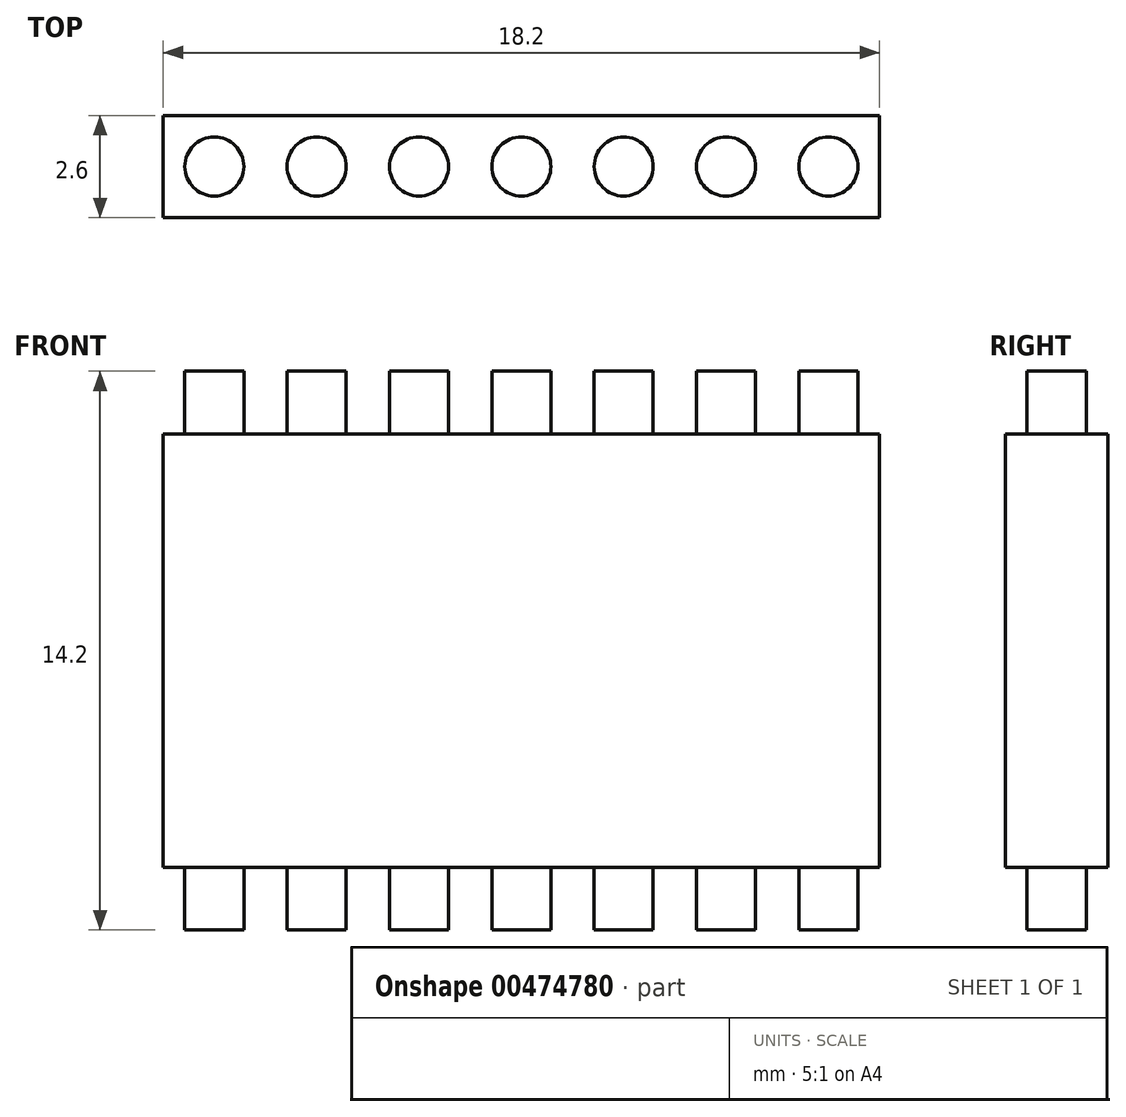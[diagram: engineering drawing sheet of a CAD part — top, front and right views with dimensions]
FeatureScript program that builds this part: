
annotation { "Feature Type Name" : "Feature", "Feature Type Description" : "" }
export const myFeature = defineFeature(function(context is Context, id is Id, definition is map)
    precondition{}
    {
        {
            var Q0;
            Q0=qCreatedBy(makeId("Top.planeOp"),FACE);
            var sketch = newSketch(context, id + "F0", { "sketchPlane" : qUnion([Q0])});
            skLineSegment(sketch, "E0.bottom", {"start": v(0, 0) * mm, "end": v(18.2, 0) * mm});
            skLineSegment(sketch, "E0.top", {"start": v(0, 2.6) * mm, "end": v(18.2, 2.6) * mm});
            skLineSegment(sketch, "E0.left", {"start": v(0, 0) * mm, "end": v(0, 2.6) * mm});
            skLineSegment(sketch, "E0.right", {"start": v(18.2, 0) * mm, "end": v(18.2, 2.6) * mm});
            skSolve(sketch);
        }
        {
            var Q0;
            Q0 = qSketchRegion(id + "F0", true);
            extrude(context, id + "F1", {"entities" : qUnion([Q0]), "depth" : 11 * mm});
        }
        {
            var Q0;
            Q0=makeQuery(id+"F1.opExtrude","CAP_FACE",FACE,{"disambiguationData":[OSD([sQuery(id+"F0.wireOp",EDGE,"E0.bottom"),sQuery(id+"F0.wireOp",EDGE,"E0.top"),sQuery(id+"F0.wireOp",EDGE,"E0.left"),sQuery(id+"F0.wireOp",EDGE,"E0.right")])],"isStart":false});
            var sketch = newSketch(context, id + "F2", { "sketchPlane" : qUnion([Q0])});
            skLineSegment(sketch, "E1", {"start": v(0, 1.3) * mm, "end": v(18.2, 1.3) * mm, "construction": true});
            skLineSegment(sketch, "E2", {"start": v(9.1, 2.6) * mm, "end": v(9.1, 0) * mm, "construction": true});
            skCircle(sketch, "E3", {"center": v(9.1, 1.3) * mm, "radius": 0.75 * mm});
            skCircle(sketch, "E4", {"center": v(1.3, 1.3) * mm, "radius": 0.75 * mm});
            skCircle(sketch, "E5", {"center": v(3.9, 1.3) * mm, "radius": 0.75 * mm});
            skCircle(sketch, "E6", {"center": v(6.5, 1.3) * mm, "radius": 0.75 * mm});
            skCircle(sketch, "E7", {"center": v(11.7, 1.3) * mm, "radius": 0.75 * mm});
            skCircle(sketch, "E8", {"center": v(14.3, 1.3) * mm, "radius": 0.75 * mm});
            skCircle(sketch, "E9", {"center": v(16.9, 1.3) * mm, "radius": 0.75 * mm});
            skSolve(sketch);
        }
        {
            var Q0;
            Q0 = qSketchRegion(id + "F2", true);
            extrude(context, id + "F3", {"entities" : qUnion([Q0]), "operationType" : NewBodyOperationType.ADD, "depth" : 1.6 * mm});
        }
        {
            var Q0;
            Q0=makeQuery(id+"F1.opExtrude","CAP_FACE",FACE,{"disambiguationData":[OSD([sQuery(id+"F0.wireOp",EDGE,"E0.bottom"),sQuery(id+"F0.wireOp",EDGE,"E0.top"),sQuery(id+"F0.wireOp",EDGE,"E0.left"),sQuery(id+"F0.wireOp",EDGE,"E0.right")])],"isStart":true});
            var sketch = newSketch(context, id + "F4", { "sketchPlane" : qUnion([Q0])});
            skLineSegment(sketch, "E10", {"start": v(9.1, 0) * mm, "end": v(9.1, -2.6) * mm, "construction": true});
            skLineSegment(sketch, "E11", {"start": v(0, -1.3) * mm, "end": v(18.2, -1.3) * mm, "construction": true});
            skCircle(sketch, "E12", {"center": v(9.1, -1.3) * mm, "radius": 0.75 * mm});
            skCircle(sketch, "E13", {"center": v(1.3, -1.3) * mm, "radius": 0.75 * mm});
            skCircle(sketch, "E14", {"center": v(3.9, -1.3) * mm, "radius": 0.75 * mm});
            skCircle(sketch, "E15", {"center": v(6.5, -1.3) * mm, "radius": 0.75 * mm});
            skCircle(sketch, "E16", {"center": v(11.7, -1.3) * mm, "radius": 0.75 * mm});
            skCircle(sketch, "E17", {"center": v(14.3, -1.3) * mm, "radius": 0.75 * mm});
            skCircle(sketch, "E18", {"center": v(16.9, -1.3) * mm, "radius": 0.75 * mm});
            skSolve(sketch);
        }
        {
            var Q0;
            Q0 = qSketchRegion(id + "F4", true);
            extrude(context, id + "F5", {"entities" : qUnion([Q0]), "operationType" : NewBodyOperationType.ADD, "depth" : 1.6 * mm});
        }
    });
